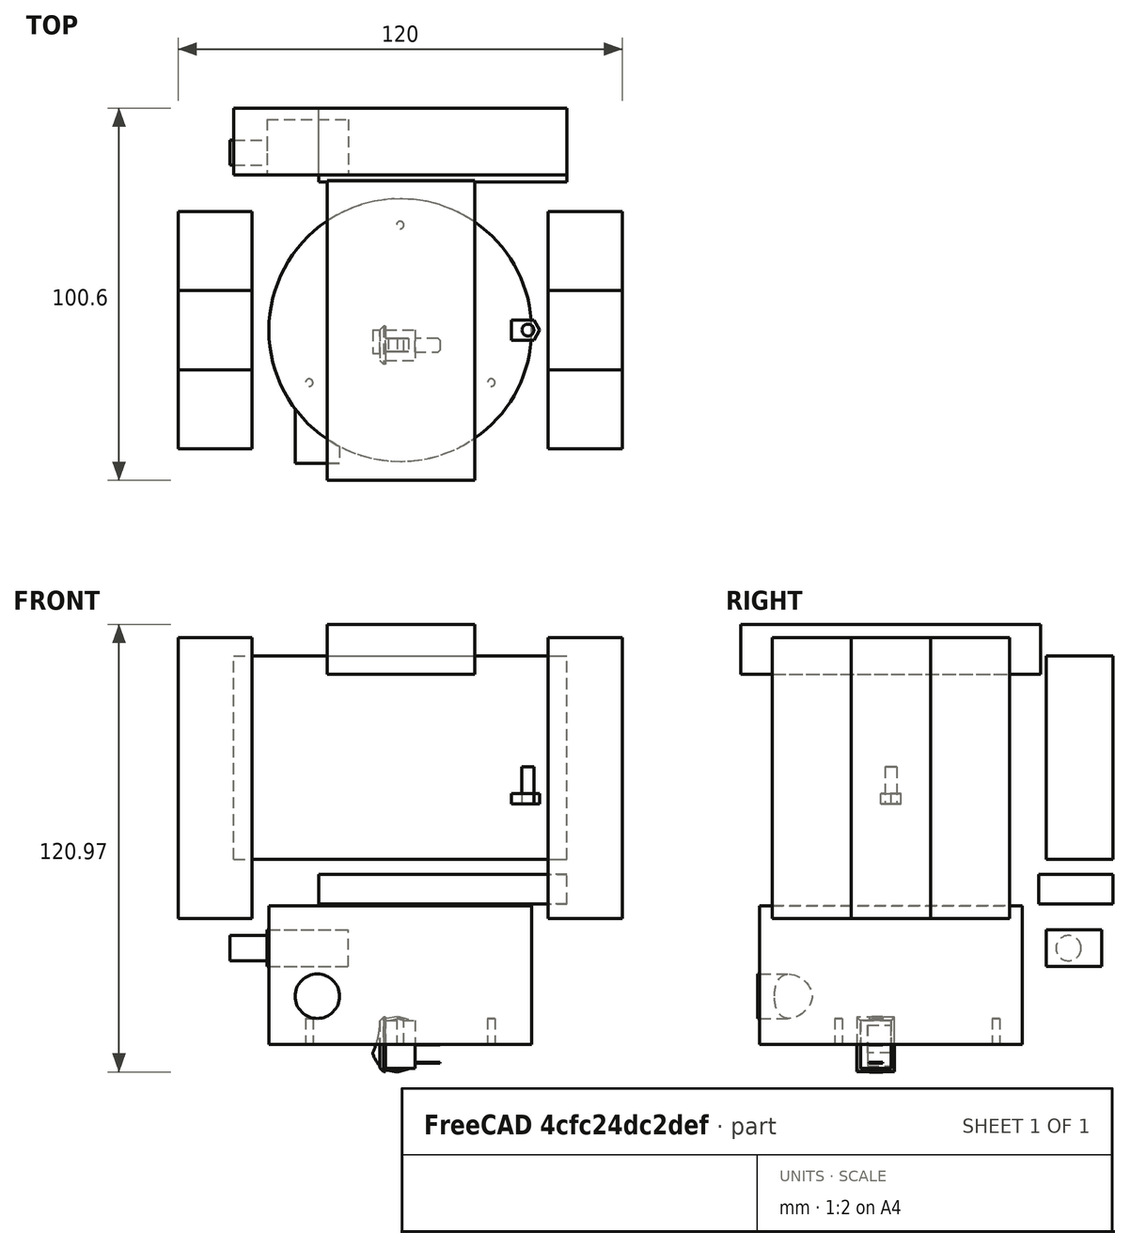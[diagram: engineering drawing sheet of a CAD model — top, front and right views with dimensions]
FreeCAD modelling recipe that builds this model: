
FCSTD DOCUMENT  (FreeCAD 0.18R4 (GitTag))
Label: ws_blower_stage
License: All rights reserved
LicenseURL: http://en.wikipedia.org/wiki/All_rights_reserved
objects: Sketcher::SketchObject×6, PartDesign::Pad×6, PartDesign::Body×6, Part::Box×4, Part::FeaturePython×2, Part::MultiFuse×2, Spreadsheet::Sheet×1, Mesh::Feature×1, Part::Feature×1, App::DocumentObjectGroup×1, Part::Cut×1, Part::Cylinder×1, App::MeasureDistance×1
note: 35 computed .brp shape members not serialized (recipe doc carries the construction recipe); baked Part::Feature solids carry a one-line shape summary decoded from their .brp

FEATURE [Spreadsheet::Sheet] Spreadsheet  label="spread"
  cells = B3=tolerance; C3(tolerance)==0.2mm; B5=case_gap; C5(case_gap)==6mm; B6=case_walls; C6(case_walls)==1mm; B8=m4_hole_d; C8(m4_hole_d)==4.2mm; B9=m3_hole_d; C9(m3_hole_d)==3.2mm
FEATURE [Sketcher::SketchObject] Sketch022
  MapMode = 5
  Placement = pos=(0,0,0) rot=(0.57735,0.57735,0.57735;2.0944rad)
  Support = -> [YZ_Plane015]
  expr: Constraints[7] = spread003.battery_h
  sketch-geometry (4):
    g0: LineSegment StartX=-10 StartY=0 StartZ=0 EndX=10 EndY=-1e-16 EndZ=0
    g1: LineSegment StartX=10 StartY=-1e-16 StartZ=0 EndX=10 EndY=67 EndZ=0
    g2: LineSegment StartX=10 StartY=67 StartZ=0 EndX=-10 EndY=67 EndZ=0
    g3: LineSegment StartX=-10 StartY=67 StartZ=0 EndX=-10 EndY=0 EndZ=0
  constraints (11):
    c: Coincident(g0,g1)
    c: Coincident(g1,g2)
    c: Coincident(g2,g3)
    c: Coincident(g3,g0)
    c: Horizontal(g2)
    c: Vertical(g1)
    c: Vertical(g3)
    c: DistanceY(g1,g1) = 67
    c: Horizontal(g0,g-1)
    c: DistanceX(g0,g0) = 20
    c: Symmetric(g0,g0,g-2)
FEATURE [PartDesign::Pad] Pad015
  Length = 8
  Length2 = 100
  Placement = pos=(0,0,0) rot=(0.57735,0.57735,0.57735;2.0944rad)
  Profile = -> Sketch022
  Reversed = true
  Type = 0
FEATURE [PartDesign::Body] Body015  label="BMS"
  Group = -> [Sketch022,Pad015]
  Origin = -> Origin015
  Placement = pos=(-22,50,38) rot=(0,1,0;1.5708rad)
  Tip = -> Pad015
FEATURE [Mesh::Feature] Can_Whole___Solid  label="Can_Whole_-_Solid"
FEATURE [Sketcher::SketchObject] Sketch040
  MapMode = 5
  Support = -> [XY_Plane028]
  expr: Constraints[1] = spread009.m3_hole_d
  sketch-geometry (1):
    g0: Circle CenterX=0 CenterY=0 CenterZ=0 NormalX=0 NormalY=0 NormalZ=1 AngleXU=0 Radius=1.6
  constraints (2):
    c: Coincident(g0,g-1)
    c: Diameter(g0) = 3.2
FEATURE [PartDesign::Pad] Pad028
  Length = 10
  Length2 = 100
  Profile = -> Sketch040
  Type = 0
FEATURE [PartDesign::Body] Body028  label="m3x10_screw003"
  Group = -> [Sketch040,Pad028]
  Origin = -> Origin028
  Placement = pos=(34.5,0,65) rot=(0,0,1;0rad)
  Tip = -> Pad028
  expr: Placement.Base.x = spread.out_d / 2 + (spread.case_gap + 2 * spread.case_walls) / 2
FEATURE [Part::Feature] Fusion002003  label="switch-1P1T003"
  Placement = pos=(0,0,0) rot=(0,1,0;4.71239rad)
  shape: bbox 18.13 x 10.2 x 14.95 mm, 47 faces (baked)
FEATURE [Sketcher::SketchObject] Sketch042
  MapMode = 5
  Support = -> [XY_Plane030]
  sketch-geometry (8):
    g0: LineSegment StartX=-1.58771 StartY=-2.75 StartZ=0 EndX=1.58771 EndY=-2.75 EndZ=0
    g1: LineSegment StartX=1.58771 StartY=-2.75 StartZ=0 EndX=3.17543 EndY=1.3e-15 EndZ=0
    g2: LineSegment StartX=3.17543 StartY=1.3e-15 StartZ=0 EndX=1.58771 EndY=2.75 EndZ=0
    g3: LineSegment StartX=1.58771 StartY=2.75 StartZ=0 EndX=-1.58771 EndY=2.75 EndZ=0
    g4: Circle [constr] CenterX=0 CenterY=0 CenterZ=0 NormalX=0 NormalY=0 NormalZ=1 AngleXU=0 Radius=3.17543
    g5: LineSegment StartX=-1.58771 StartY=2.75 StartZ=0 EndX=-4.5 EndY=2.75 EndZ=0
    g6: LineSegment StartX=-4.5 StartY=2.75 StartZ=0 EndX=-4.5 EndY=-2.75 EndZ=0
    g7: LineSegment StartX=-4.5 StartY=-2.75 StartZ=0 EndX=-1.58771 EndY=-2.75 EndZ=0
  constraints (23):
    c: Coincident(g0,g1)
    c: Coincident(g1,g2)
    c: Coincident(g2,g3)
    c: PointOnObject(g0,g4)
    c: PointOnObject(g0,g4)
    c: PointOnObject(g1,g4)
    c: PointOnObject(g2,g4)
    c: PointOnObject(g3,g4)
    c: Coincident(g4,g-1)
    c: DistanceY(g0,g2) = 5.5
    c: Coincident(g3,g5)
    c: Horizontal(g5)
    c: Coincident(g5,g6)
    c: Vertical(g6)
    c: Coincident(g6,g7)
    c: Coincident(g7,g0)
    c: Horizontal(g7)
    c: Equal(g3,g0)
    c: Horizontal(g0)
    c: Horizontal(g3)
    c: Equal(g3,g2)
    c: Equal(g2,g1)
    c: Equal(g1,g0)
FEATURE [PartDesign::Pad] Pad037
  Length = 2.8
  Length2 = 100
  Profile = -> Sketch042
  Type = 0
FEATURE [PartDesign::Body] Body030  label="m3_hex_nut001"
  Group = -> [Sketch042,Pad037]
  Origin = -> Origin030
  Placement = pos=(34.5,0,65) rot=(0,0,1;0rad)
  Tip = -> Pad037
  expr: Placement.Base.x = spread.out_d / 2 + (spread.case_gap + 2 * spread.case_walls) / 2
FEATURE [Part::Box] Box  label="Driver"
  AttacherType = Attacher::AttachEngine3D
  Height = 18
  Length = 90
  Placement = pos=(-45,60,50) rot=(1,0,0;1.5708rad)
  Width = 55
FEATURE [App::DocumentObjectGroup] Group  label="electronics"
  Group = -> [Body015,Fusion002003,Box]
FEATURE [Part::Box] Box001  label="hepa_filter"
  AttacherType = Attacher::AttachEngine3D
  Height = 13.5
  Length = 81
  Placement = pos=(20.2,-40.6,100) rot=(0,0,1;1.5708rad)
  Width = 40
  expr: Placement.Base.x = 40.4 / 2
  expr: Placement.Base.y = -81.2 / 2
FEATURE [Part::Box] Box002  label="battery_holder"
  AttacherType = Attacher::AttachEngine3D
  Height = 20
  Length = 76
  Width = 21.4
FEATURE [Sketcher::SketchObject] Sketch
  MapMode = 5
  Support = -> [XY_Plane031]
  sketch-geometry (1):
    g0: Circle CenterX=0 CenterY=0 CenterZ=0 NormalX=0 NormalY=0 NormalZ=1 AngleXU=0 Radius=35.5
  constraints (2):
    c: Coincident(g0,g-1)
    c: Diameter(g0) = 71
FEATURE [PartDesign::Pad] Pad
  Length = 37.5
  Length2 = 100
  Profile = -> Sketch
  Type = 0
FEATURE [PartDesign::Body] Body031
  Group = -> [Sketch,Pad]
  Origin = -> Origin031
  Tip = -> Pad
FEATURE [Sketcher::SketchObject] Sketch052
  MapMode = 5
  Placement = pos=(0,0,0) rot=(1,0,0;1.5708rad)
  Support = -> [XZ_Plane032]
  sketch-geometry (1):
    g0: Circle CenterX=-22.4 CenterY=13 CenterZ=0 NormalX=0 NormalY=0 NormalZ=1 AngleXU=0 Radius=6
  constraints (3):
    c: DistanceY(g-1,g0) = 13
    c: DistanceX(g0,g-1) = 22.4
    c: Diameter(g0) = 12
FEATURE [PartDesign::Pad] Pad039
  Length = 36
  Length2 = 100
  Placement = pos=(0,0,0) rot=(1,0,0;1.5708rad)
  Profile = -> Sketch052
  Type = 0
FEATURE [PartDesign::Body] Body032
  Group = -> [Sketch052,Pad039]
  Origin = -> Origin032
  Tip = -> Pad039
FEATURE [Sketcher::SketchObject] Sketch053
  MapMode = 5
  Support = -> [XY_Plane033]
  expr: Constraints[2] = 56.8 / 2
  sketch-geometry (1):
    g0: Circle CenterX=0 CenterY=28.4 CenterZ=0 NormalX=0 NormalY=0 NormalZ=1 AngleXU=0 Radius=1
  constraints (3):
    c: PointOnObject(g0,g-2)
    c: Diameter(g0) = 2
    c: DistanceY(g-1,g0) = 28.4
FEATURE [PartDesign::Pad] Pad040
  Length = 7
  Length2 = 100
  Profile = -> Sketch053
  Type = 0
FEATURE [PartDesign::Body] Body033
  Group = -> [Sketch053,Pad040]
  Origin = -> Origin033
  Tip = -> Pad040
FEATURE [Part::FeaturePython] Array  # Draft array (typed FeaturePython)
  Angle = 360
  ArrayType = 1
  Axis = (0,0,1)
  Base = -> Body033
  Center = (0,0,0)
  Fuse = false
  IntervalAxis = (0,0,0)
  IntervalX = (1,0,0)
  IntervalY = (0,1,0)
  IntervalZ = (0,0,1)
  NumberPolar = 3
  NumberX = 1
  NumberY = 1
  NumberZ = 1
FEATURE [Part::MultiFuse] Fusion
  Shapes = -> [Body031,Body032]
FEATURE [Part::Cut] Cut  label="blower"
  Base = -> Fusion
  Tool = -> Array
FEATURE [Part::FeaturePython] Array001  label="battery_array"  # Draft array (typed FeaturePython)
  Angle = 360
  ArrayType = 0
  Axis = (1,0,0)
  Base = -> Box002
  Center = (0,0,0)
  Fuse = false
  IntervalAxis = (0,0,0)
  IntervalX = (0,0,0)
  IntervalY = (0,21.4,0)
  IntervalZ = (0,0,-100)
  NumberPolar = 1
  NumberX = 2
  NumberY = 3
  NumberZ = 2
  Placement = pos=(40,-32.1,110) rot=(0,1,0;1.5708rad)
  expr: Placement.Base.y = -21.4 * 3 / 2
FEATURE [Part::Box] Box003  label="Cube"
  AttacherType = Attacher::AttachEngine3D
  Height = 15
  Length = 22
  Width = 10
FEATURE [Part::Cylinder] Cylinder
  Angle = 360
  AttacherType = Attacher::AttachEngine3D
  Height = 10
  Placement = pos=(-10,5,9) rot=(0,1,0;1.5708rad)
  Radius = 3.4
FEATURE [Part::MultiFuse] Fusion002004  label="potentiometer"
  Placement = pos=(-36,57,21) rot=(1,0,0;1.5708rad)
  Shapes = -> [Box003,Cylinder]
FEATURE [App::MeasureDistance] Distance  label="Distance: 22,19 mm"
  Distance = 22.1932
  P1 = (-40,-32.1,110)
  P2 = (-19.8,-40.6,113.5)
